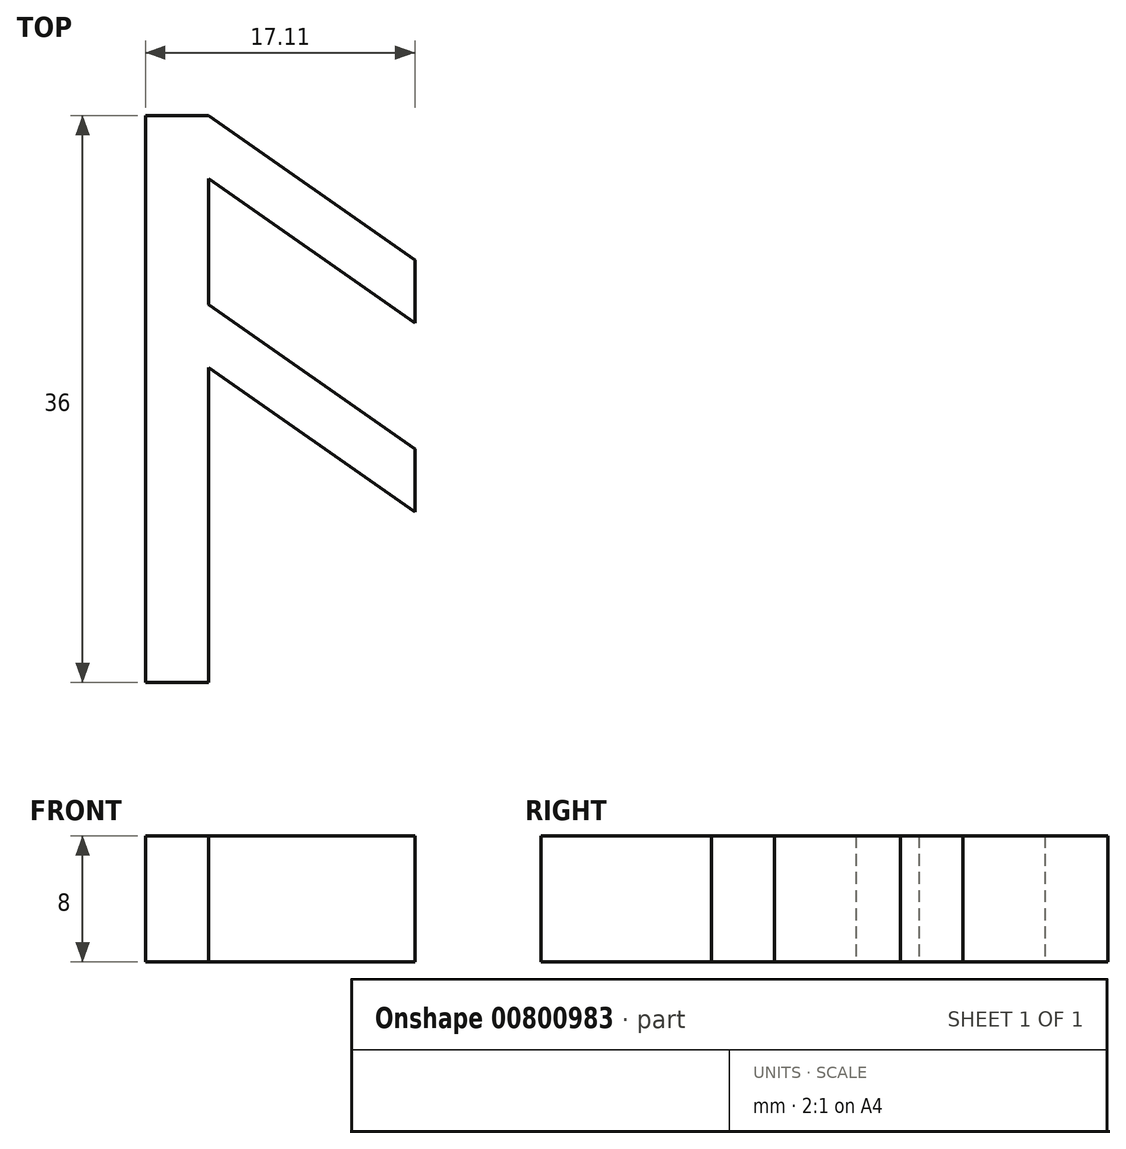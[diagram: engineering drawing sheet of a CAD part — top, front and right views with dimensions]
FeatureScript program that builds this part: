
annotation { "Feature Type Name" : "Feature", "Feature Type Description" : "" }
export const myFeature = defineFeature(function(context is Context, id is Id, definition is map)
    precondition{}
    {
        {
            var Q0;
            Q0=qCreatedBy(makeId("Top.planeOp"),FACE);
            var sketch = newSketch(context, id + "F0", { "sketchPlane" : qUnion([Q0])});
            skLineSegment(sketch, "E0", {"start": v(0, 0) * mm, "end": v(0, -36) * mm});
            skLineSegment(sketch, "E1", {"start": v(0, -36) * mm, "end": v(4, -36) * mm});
            skLineSegment(sketch, "E2", {"start": v(4, -36) * mm, "end": v(4, -16) * mm});
            skLineSegment(sketch, "E3", {"start": v(4, -16) * mm, "end": v(17.1, -25.18) * mm});
            skLineSegment(sketch, "E4", {"start": v(17.1, -25.18) * mm, "end": v(17.1, -21.18) * mm});
            skLineSegment(sketch, "E5", {"start": v(17.1, -21.18) * mm, "end": v(4, -12) * mm});
            skLineSegment(sketch, "E6", {"start": v(4, -12) * mm, "end": v(4, -4) * mm});
            skLineSegment(sketch, "E7", {"start": v(4, -4) * mm, "end": v(17.1, -13.18) * mm});
            skLineSegment(sketch, "E8", {"start": v(17.1, -13.18) * mm, "end": v(17.1, -9.18) * mm});
            skLineSegment(sketch, "E9", {"start": v(17.1, -9.18) * mm, "end": v(4, 0) * mm});
            skLineSegment(sketch, "E10", {"start": v(4, 0) * mm, "end": v(0, 0) * mm});
            skSolve(sketch);
        }
        {
            var Q0;
            Q0=makeQuery(id+"F0.imprint","IMPRINT",FACE,{"disambiguationData":[TD([[makeQuery(id+"F0.imprint","IMPRINT",EDGE,{"derivedFrom":sQuery(id+"F0.wireOp",EDGE,"E0")}),1.0]])]});
            extrude(context, id + "F1", {"entities" : qUnion([Q0]), "depth" : 8 * mm, "offsetDistance" : 25 * mm});
        }
    });
